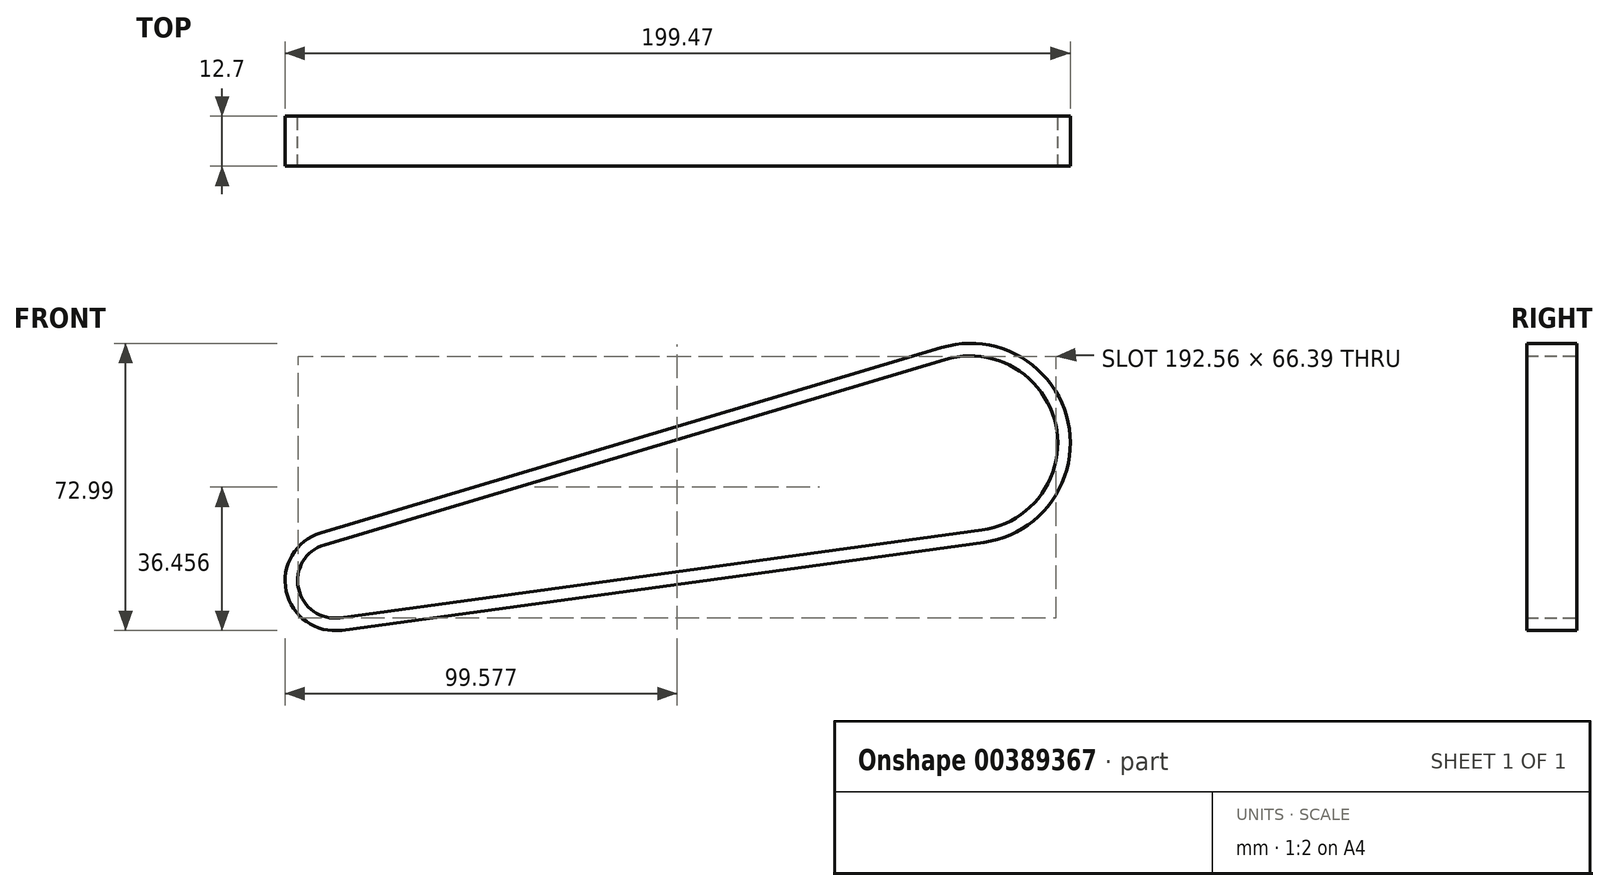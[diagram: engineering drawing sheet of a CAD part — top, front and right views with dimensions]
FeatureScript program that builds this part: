
annotation { "Feature Type Name" : "Feature", "Feature Type Description" : "" }
export const myFeature = defineFeature(function(context is Context, id is Id, definition is map)
    precondition{}
    {
        {
            var Q0;
            Q0=qCreatedBy(makeId("Front.planeOp"),FACE);
            var sketch = newSketch(context, id + "F0", { "sketchPlane" : qUnion([Q0])});
            skArc(sketch, "E0", {"start": v(125.85, 12.87) * mm, "mid": v(144.56, 39.59) * mm, "end": v(116.49, 56.19) * mm});
            skArc(sketch, "E1", {"start": v(-41.25, 9.13) * mm, "mid": v(-47.84, -2.01) * mm, "end": v(-37.24, -9.44) * mm});
            skLineSegment(sketch, "E2", {"start": v(-41.25, 9.13) * mm, "end": v(116.49, 56.19) * mm});
            skLineSegment(sketch, "E3", {"start": v(-37.24, -9.44) * mm, "end": v(125.85, 12.87) * mm});
            skArc(sketch, "E4", {"start": v(-42.16, 12.17) * mm, "mid": v(-50.94, -2.68) * mm, "end": v(-36.8, -12.58) * mm});
            skArc(sketch, "E5", {"start": v(126.28, 9.72) * mm, "mid": v(147.67, 40.26) * mm, "end": v(115.58, 59.23) * mm});
            skLineSegment(sketch, "E6", {"start": v(-42.16, 12.17) * mm, "end": v(115.58, 59.23) * mm});
            skLineSegment(sketch, "E7", {"start": v(-36.8, -12.58) * mm, "end": v(126.28, 9.72) * mm});
            skSolve(sketch);
        }
        {
            var Q0;
            Q0 = qSketchRegion(id + "F0", true);
            extrude(context, id + "F1", {"entities" : qUnion([Q0]), "depth" : 12.7 * mm});
        }
    });
